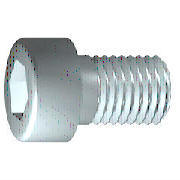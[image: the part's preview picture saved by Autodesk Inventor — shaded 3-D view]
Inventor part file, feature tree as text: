
AUTODESK INVENTOR PART (.ipt)
format: ipt  version: 2020 (Build 240168000, 168)  size: 195,584 bytes
history: native  units: mm (DEFAULTED — no unit token found)
features: sketch x2, extrude x1, plane x1, fillet x1
ambient origin geometry x7: Origin, YZ Plane, XY Plane, X Axis, Y Axis, Z Axis, Center Point
bodies: Solid1 (feature_tree)
feature tree (5):
  extrude  "슬롯"  Depth=14.0mm
  plane  "Work Plane1"
  fillet  "Fillet2"  Radius=0.49086mm
  sketch  "스케치1"
  sketch  "스케치2"
